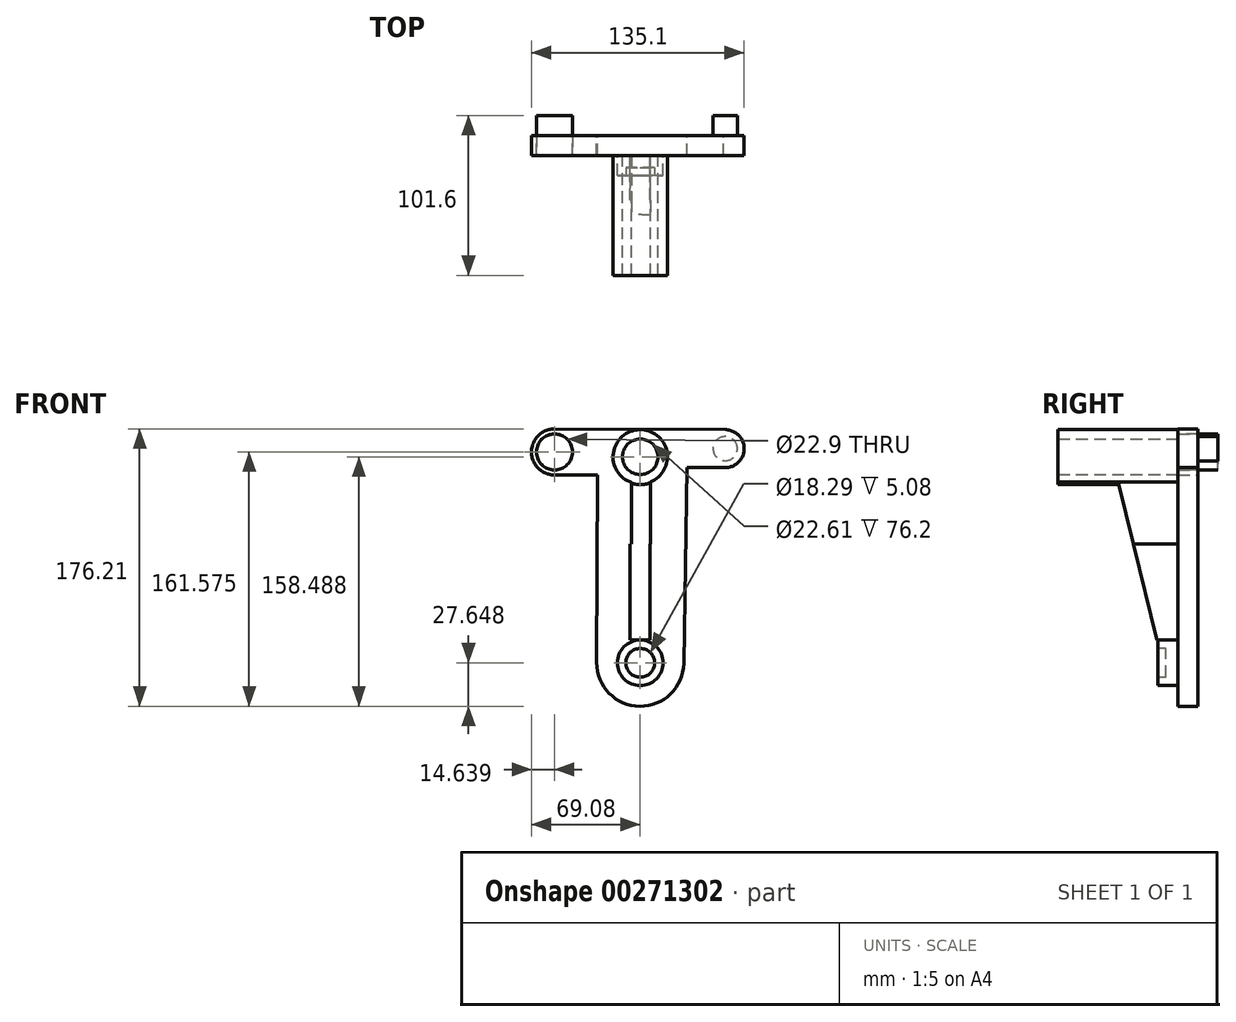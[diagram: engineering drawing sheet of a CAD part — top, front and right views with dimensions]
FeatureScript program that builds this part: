
annotation { "Feature Type Name" : "Feature", "Feature Type Description" : "" }
export const myFeature = defineFeature(function(context is Context, id is Id, definition is map)
    precondition{}
    {
        {
            var Q0;
            Q0=qCreatedBy(makeId("Front.planeOp"),FACE);
            var sketch = newSketch(context, id + "F0", { "sketchPlane" : qUnion([Q0])});
            skCircle(sketch, "E0", {"center": v(0, 55.26) * mm, "radius": 11.46 * mm});
            skCircle(sketch, "E1", {"center": v(0, 55.26) * mm, "radius": 17.26 * mm});
            skLineSegment(sketch, "E2", {"start": v(-5.44, 38.88) * mm, "end": v(-5.44, 0) * mm});
            skLineSegment(sketch, "E3", {"start": v(-5.44, 0) * mm, "end": v(6.37, -0.2) * mm});
            skLineSegment(sketch, "E4", {"start": v(6.37, -0.2) * mm, "end": v(6.37, 39.22) * mm});
            skSolve(sketch);
        }
        {
            var Q0;
            Q0 = qSketchRegion(id + "F0", true);
            extrude(context, id + "F1", {"entities" : qUnion([Q0]), "depth" : 50.8 * mm});
        }
        {
            var Q0;
            Q0=qCreatedBy(makeId("Front.planeOp"),FACE);
            var sketch = newSketch(context, id + "F2", { "sketchPlane" : qUnion([Q0])});
            skArc(sketch, "E5", {"start": v(52.88, 48.45) * mm, "mid": v(66, 59.87) * mm, "end": v(54.04, 72.49) * mm});
            skCircle(sketch, "E6", {"center": v(-54.44, 58.34) * mm, "radius": 14.63 * mm});
            skCircle(sketch, "E7", {"center": v(-54.44, 58.34) * mm, "radius": 9.16 * mm});
            skCircle(sketch, "E8", {"center": v(-54.44, 58.34) * mm, "radius": 11.45 * mm});
            skCircle(sketch, "E9", {"center": v(53.98, 60.45) * mm, "radius": 7.7 * mm});
            skCircle(sketch, "E10", {"center": v(53.98, 60.45) * mm, "radius": 5.27 * mm});
            skLineSegment(sketch, "E11", {"start": v(-54.25, 72.98) * mm, "end": v(54.04, 72.49) * mm});
            skCircle(sketch, "E12", {"center": v(0, -75.58) * mm, "radius": 27.64 * mm});
            skLineSegment(sketch, "E13", {"start": v(55.08, 48.45) * mm, "end": v(29.73, 48.45) * mm});
            skLineSegment(sketch, "E14", {"start": v(29.73, 48.45) * mm, "end": v(27.62, -77.16) * mm});
            skLineSegment(sketch, "E15", {"start": v(-55.07, 43.71) * mm, "end": v(-27.08, 43.71) * mm});
            skLineSegment(sketch, "E16", {"start": v(-27.08, 43.71) * mm, "end": v(-27.65, -77.16) * mm});
            skSolve(sketch);
        }
        {
            var Q0;
            Q0 = qSketchRegion(id + "F2", true);
            extrude(context, id + "F3", {"entities" : qUnion([Q0]), "operationType" : NewBodyOperationType.ADD, "depth" : 12.7 * mm});
        }
        {
            var Q0;
            {var subQ0=sQuery(id+"F2.wireOp",EDGE,"E12");var subQ1=sQuery(id+"F2.wireOp",EDGE,"E5");var subQ2=sQuery(id+"F2.wireOp",EDGE,"E11");var subQ3=sQuery(id+"F2.wireOp",EDGE,"E9");var subQ4=sQuery(id+"F2.wireOp",EDGE,"E8");var subQ5=sQuery(id+"F2.wireOp",EDGE,"E6");var subQ6=sQuery(id+"F2.wireOp",EDGE,"E15");var subQ7=sQuery(id+"F2.wireOp",EDGE,"E13");var subQ8=sQuery(id+"F2.wireOp",EDGE,"E14");var subQ9=sQuery(id+"F2.wireOp",EDGE,"E16");Q0=makeQuery(id+"F3.boolean.opBoolean","SPLIT",FACE,{"disambiguationData":[TD([makeQuery(id+"F1.opExtrude","SWEPT_FACE",FACE,{"disambiguationData":[OSD([sQuery(id+"F0.wireOp",EDGE,"E1")])]})])],"derivedFrom":makeQuery(id+"F3.opExtrude","CAP_FACE",FACE,{"disambiguationData":[OSD([subQ1,subQ5,subQ4,subQ3,subQ2,subQ0,subQ7,subQ8,subQ6,subQ9])],"isStart":false})});}
            var sketch = newSketch(context, id + "F4", { "sketchPlane" : qUnion([Q0])});
            skCircle(sketch, "E17", {"center": v(0, -75.58) * mm, "radius": 14.5 * mm});
            skSolve(sketch);
        }
        {
            var Q0;
            Q0 = qSketchRegion(id + "F4", true);
            extrude(context, id + "F5", {"entities" : qUnion([Q0]), "operationType" : NewBodyOperationType.ADD, "depth" : 12.7 * mm});
        }
        {
            var Q0;
            Q0=makeQuery(id+"F5.opExtrude","CAP_FACE",FACE,{"disambiguationData":[OSD([sQuery(id+"F4.wireOp",EDGE,"E17")])],"isStart":false});
            var sketch = newSketch(context, id + "F6", { "sketchPlane" : qUnion([Q0])});
            skCircle(sketch, "E18", {"center": v(0, -75.58) * mm, "radius": 9.15 * mm});
            skSolve(sketch);
        }
        {
            var Q0;
            Q0=makeQuery(id+"F6.imprint","IMPRINT",FACE,{"disambiguationData":[TD([[makeQuery(id+"F6.imprint","IMPRINT",EDGE,{"derivedFrom":sQuery(id+"F6.wireOp",EDGE,"E18")}),1.0]])]});
            extrude(context, id + "F7", {"entities" : qUnion([Q0]), "operationType" : NewBodyOperationType.REMOVE, "oppositeDirection" : true, "depth" : 5.08 * mm});
        }
        {
            var Q0;
            Q0=qCreatedBy(makeId("Right.planeOp"),FACE);
            var sketch = newSketch(context, id + "F8", { "sketchPlane" : qUnion([Q0])});
            skLineSegment(sketch, "E19.bottom", {"start": v(-50.48, 0) * mm, "end": v(-12.6, 0) * mm});
            skLineSegment(sketch, "E19.top", {"start": v(-50.48, -61.02) * mm, "end": v(-12.6, -61.02) * mm});
            skLineSegment(sketch, "E19.left", {"start": v(-50.48, 0) * mm, "end": v(-50.48, -61.02) * mm});
            skLineSegment(sketch, "E19.right", {"start": v(-12.6, 0) * mm, "end": v(-12.6, -61.02) * mm});
            skSolve(sketch);
        }
        {
            var Q0;
            Q0=makeQuery(id+"F8.imprint","IMPRINT",FACE,{"disambiguationData":[TD([[makeQuery(id+"F8.imprint","IMPRINT",EDGE,{"derivedFrom":sQuery(id+"F8.wireOp",EDGE,"E19.bottom")}),-1.0]])]});
            extrude(context, id + "F9", {"entities" : qUnion([Q0]), "operationType" : NewBodyOperationType.ADD, "endBound" : BoundingType.SYMMETRIC, "depth" : 12.7 * mm});
        }
        {
            var Q0;
            Q0=makeQuery(id+"F1.opExtrude","SWEPT_FACE",FACE,{"disambiguationData":[OSD([sQuery(id+"F0.wireOp",EDGE,"E4")])]});
            var sketch = newSketch(context, id + "F10", { "sketchPlane" : qUnion([Q0])});
            skLineSegment(sketch, "E20", {"start": v(-25.88, -61.25) * mm, "end": v(-50.8, 39.22) * mm});
            skLineSegment(sketch, "E21", {"start": v(-50.8, 39.22) * mm, "end": v(-51, -61.82) * mm});
            skLineSegment(sketch, "E22", {"start": v(-51, -61.82) * mm, "end": v(-25.88, -61.25) * mm});
            skSolve(sketch);
        }
        {
            var Q0;
            Q0=makeQuery(id+"F10.imprint","IMPRINT",FACE,{"disambiguationData":[TD([[makeQuery(id+"F10.imprint","IMPRINT",EDGE,{"derivedFrom":sQuery(id+"F10.wireOp",EDGE,"E21")}),1.0]])]});
            var Q1;
            {var subQ1=sQuery(id+"F0.wireOp",EDGE,"E4");var subQ2=makeQuery(id+"F1.opExtrude","CAP_EDGE",EDGE,{"disambiguationData":[OSD([subQ1])],"isStart":false});Q1=makeQuery(id+"F10.imprint","IMPRINT",FACE,{"disambiguationData":[TD([[makeQuery(id+"F10.imprint","IMPRINT",EDGE,{"derivedFrom":subQ2}),-1.0]])]});}
            extrude(context, id + "F11", {"entities" : qUnion([Q0, Q1]), "operationType" : NewBodyOperationType.REMOVE, "oppositeDirection" : true, "depth" : 25.4 * mm});
        }
        {
            var Q0;
            {var subQ0=sQuery(id+"F2.wireOp",EDGE,"E12");var subQ1=sQuery(id+"F2.wireOp",EDGE,"E5");var subQ2=sQuery(id+"F2.wireOp",EDGE,"E11");var subQ3=sQuery(id+"F2.wireOp",EDGE,"E9");var subQ4=sQuery(id+"F2.wireOp",EDGE,"E8");var subQ5=sQuery(id+"F2.wireOp",EDGE,"E6");var subQ6=sQuery(id+"F2.wireOp",EDGE,"E15");var subQ7=sQuery(id+"F2.wireOp",EDGE,"E13");var subQ8=sQuery(id+"F2.wireOp",EDGE,"E14");var subQ9=sQuery(id+"F2.wireOp",EDGE,"E16");Q0=makeQuery(id+"F3.boolean.opBoolean","SPLIT",FACE,{"disambiguationData":[TD([makeQuery(id+"F1.opExtrude","SWEPT_FACE",FACE,{"disambiguationData":[OSD([sQuery(id+"F0.wireOp",EDGE,"E1")])]})])],"derivedFrom":makeQuery(id+"F3.opExtrude","CAP_FACE",FACE,{"disambiguationData":[OSD([subQ1,subQ5,subQ4,subQ3,subQ2,subQ0,subQ7,subQ8,subQ6,subQ9])],"isStart":false})});}
            var sketch = newSketch(context, id + "F12", { "sketchPlane" : qUnion([Q0])});
            skCircle(sketch, "E23", {"center": v(0, 55.26) * mm, "radius": 17.7 * mm});
            skCircle(sketch, "E24", {"center": v(0, 55.26) * mm, "radius": 11.3 * mm});
            skSolve(sketch);
        }
        {
            var Q0;
            Q0=makeQuery(id+"F12.imprint","IMPRINT",FACE,{"disambiguationData":[TD([[makeQuery(id+"F12.imprint","IMPRINT",EDGE,{"derivedFrom":sQuery(id+"F12.wireOp",EDGE,"E24")}),-1.0]])]});
            extrude(context, id + "F13", {"entities" : qUnion([Q0]), "operationType" : NewBodyOperationType.ADD, "depth" : 76.2 * mm});
        }
        {
            var Q0;
            {var subQ0=sQuery(id+"F2.wireOp",EDGE,"E12");var subQ1=sQuery(id+"F2.wireOp",EDGE,"E5");var subQ2=sQuery(id+"F2.wireOp",EDGE,"E11");var subQ3=sQuery(id+"F2.wireOp",EDGE,"E9");var subQ4=sQuery(id+"F2.wireOp",EDGE,"E8");var subQ5=sQuery(id+"F2.wireOp",EDGE,"E6");var subQ6=sQuery(id+"F2.wireOp",EDGE,"E15");var subQ7=sQuery(id+"F2.wireOp",EDGE,"E13");var subQ8=sQuery(id+"F2.wireOp",EDGE,"E14");var subQ9=sQuery(id+"F2.wireOp",EDGE,"E16");Q0=makeQuery(id+"F3.boolean.opBoolean","SPLIT",FACE,{"disambiguationData":[TD([makeQuery(id+"F1.opExtrude","SWEPT_FACE",FACE,{"disambiguationData":[OSD([sQuery(id+"F0.wireOp",EDGE,"E1")])]})])],"derivedFrom":makeQuery(id+"F3.opExtrude","CAP_FACE",FACE,{"disambiguationData":[OSD([subQ1,subQ5,subQ4,subQ3,subQ2,subQ0,subQ7,subQ8,subQ6,subQ9])],"isStart":false})});}
            var sketch = newSketch(context, id + "F14", { "sketchPlane" : qUnion([Q0])});
            skCircle(sketch, "E25", {"center": v(53.98, 60.45) * mm, "radius": 8.48 * mm});
            skCircle(sketch, "E26", {"center": v(-54.44, 58.34) * mm, "radius": 11.43 * mm});
            skSolve(sketch);
        }
        {
            var Q0;
            Q0=makeQuery(id+"F14.imprint","IMPRINT",FACE,{"disambiguationData":[TD([[makeQuery(id+"F14.imprint","IMPRINT",EDGE,{"derivedFrom":sQuery(id+"F14.wireOp",EDGE,"E26")}),1.0]])]});
            var Q1;
            Q1=makeQuery(id+"F14.imprint","IMPRINT",FACE,{"disambiguationData":[TD([[makeQuery(id+"F14.imprint","IMPRINT",EDGE,{"derivedFrom":makeQuery(id+"F3.opExtrude","CAP_EDGE",EDGE,{"disambiguationData":[OSD([sQuery(id+"F2.wireOp",EDGE,"E9")])],"isStart":false})}),1.0]])]});
            extrude(context, id + "F15", {"entities" : qUnion([Q0, Q1]), "operationType" : NewBodyOperationType.ADD, "oppositeDirection" : true, "depth" : 25.4 * mm});
        }
    });
